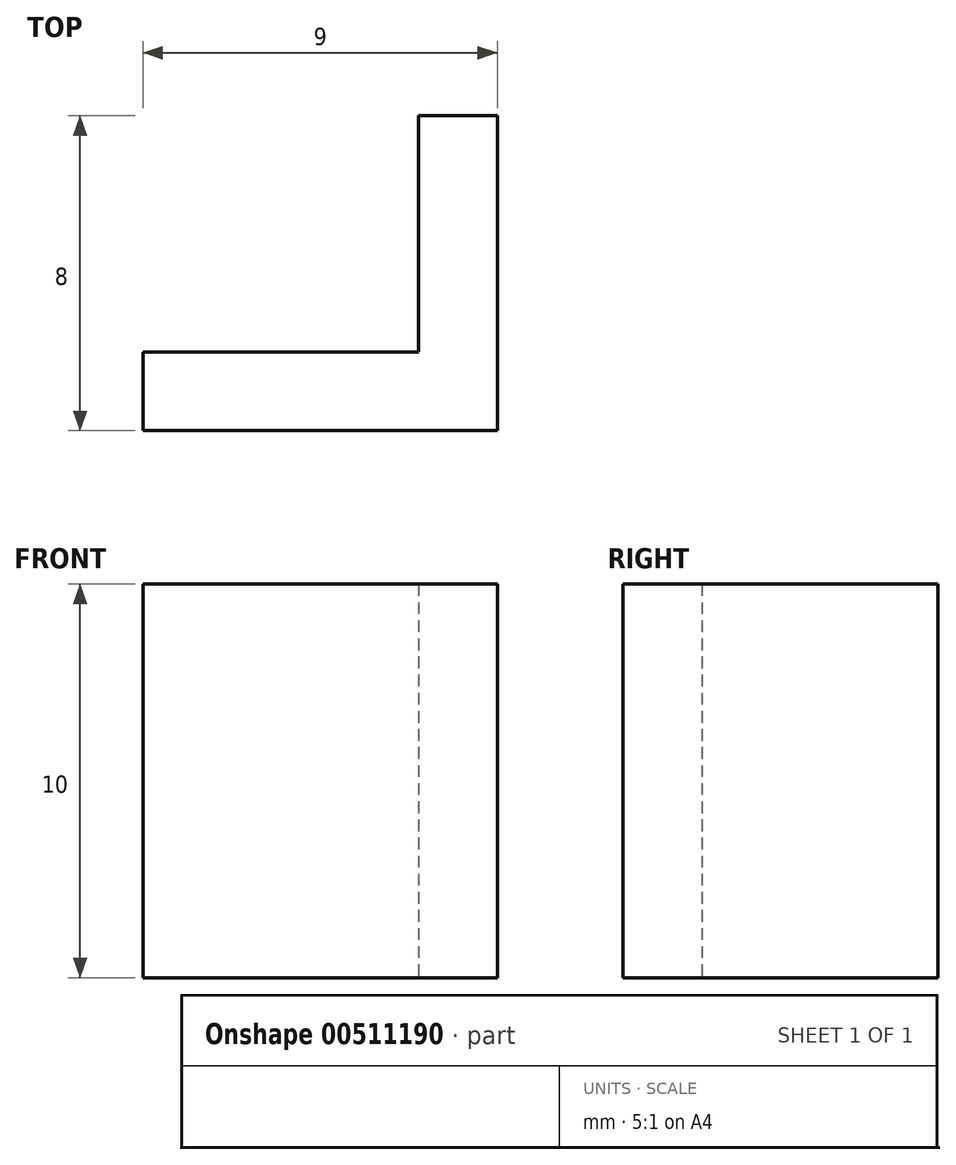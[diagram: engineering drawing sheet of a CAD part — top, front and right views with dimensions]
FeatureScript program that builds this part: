
annotation { "Feature Type Name" : "Feature", "Feature Type Description" : "" }
export const myFeature = defineFeature(function(context is Context, id is Id, definition is map)
    precondition{}
    {
        {
            var Q0;
            Q0=qCreatedBy(makeId("Top.planeOp"),FACE);
            var sketch = newSketch(context, id + "F0", { "sketchPlane" : qUnion([Q0])});
            skLineSegment(sketch, "E0.top", {"start": v(-4, -3.33) * mm, "end": v(3, -3.33) * mm});
            skLineSegment(sketch, "E0.right", {"start": v(3, 2.67) * mm, "end": v(3, -3.33) * mm});
            skLineSegment(sketch, "E1.top", {"start": v(-4, -5.33) * mm, "end": v(5, -5.33) * mm});
            skLineSegment(sketch, "E1.right", {"start": v(5, 2.67) * mm, "end": v(5, -5.33) * mm});
            skLineSegment(sketch, "E2", {"start": v(-4, -3.33) * mm, "end": v(-4, -5.33) * mm});
            skLineSegment(sketch, "E3", {"start": v(3, 2.67) * mm, "end": v(5, 2.67) * mm});
            skSolve(sketch);
        }
        {
            var Q0;
            Q0=makeQuery(id+"F0.imprint","IMPRINT",FACE,{"disambiguationData":[TD([[makeQuery(id+"F0.imprint","IMPRINT",EDGE,{"derivedFrom":sQuery(id+"F0.wireOp",EDGE,"E0.top")}),-1.0]])]});
            extrude(context, id + "F1", {"entities" : qUnion([Q0]), "depth" : 10 * mm});
        }
    });
